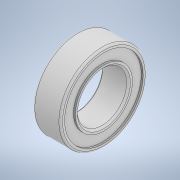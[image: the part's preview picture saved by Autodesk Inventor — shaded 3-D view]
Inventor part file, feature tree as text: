
AUTODESK INVENTOR PART (.ipt)
format: ipt  version: 2020 (Build 240168000, 168)  size: 161,792 bytes
history: native  units: in
note: dims shown in document units (in); Inventor stores cm internally (conversion verified against a paired STEP export)
features: revolve x1
ambient origin geometry x8: Origin, YZ Plane, XZ Plane, XY Plane, X Axis, Y Axis, Z Axis, Center Point
bodies: Solid1 (feature_tree)
feature tree (1):
  revolve  "Revolve1"  [1 undecoded]
note: 1 required parameter value undecoded (feature->parameter linkage not recoverable at this tier; creation-order binding heuristic only, values carry confidence <= 0.55)
